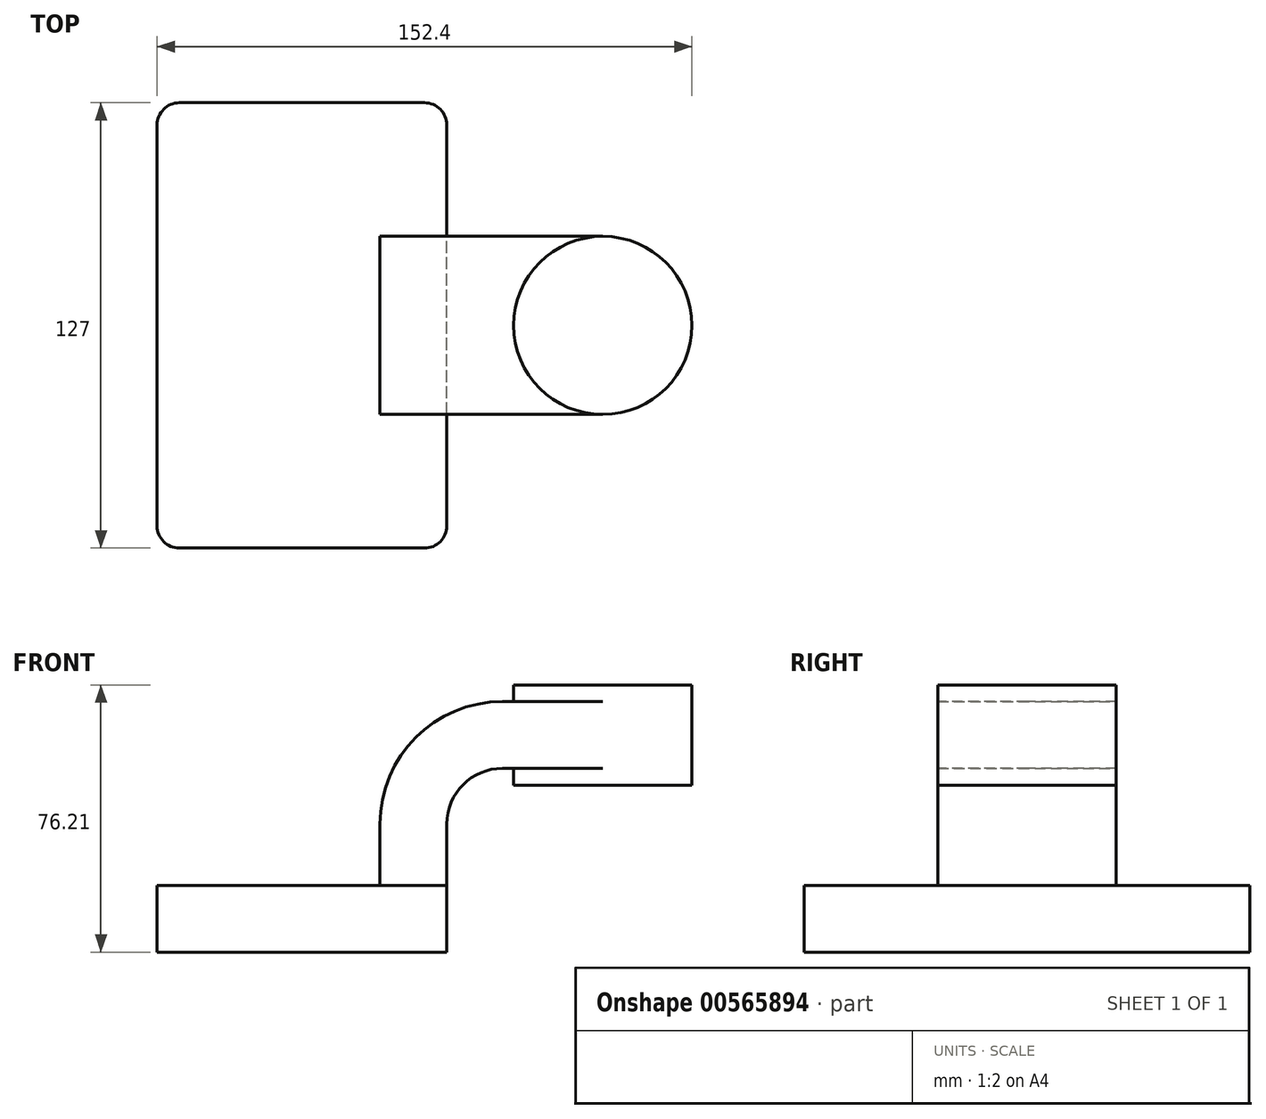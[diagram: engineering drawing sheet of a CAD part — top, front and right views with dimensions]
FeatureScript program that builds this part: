
annotation { "Feature Type Name" : "Feature", "Feature Type Description" : "" }
export const myFeature = defineFeature(function(context is Context, id is Id, definition is map)
    precondition{}
    {
        {
            var Q0;
            Q0=qCreatedBy(makeId("Front.planeOp"),FACE);
            var sketch = newSketch(context, id + "F0", { "sketchPlane" : qUnion([Q0])});
            skLineSegment(sketch, "E0.bottom", {"start": v(-41.28, -9.53) * mm, "end": v(41.28, -9.53) * mm});
            skLineSegment(sketch, "E0.top", {"start": v(-41.28, 9.52) * mm, "end": v(41.28, 9.52) * mm});
            skLineSegment(sketch, "E0.left", {"start": v(-41.28, -9.53) * mm, "end": v(-41.28, 9.52) * mm});
            skLineSegment(sketch, "E0.right", {"start": v(41.28, -9.53) * mm, "end": v(41.28, 9.52) * mm});
            skPoint(sketch, "E0.middle", {"position": v(0, 0) * mm});
            skLineSegment(sketch, "E1.bottom", {"start": v(60.32, 38.1) * mm, "end": v(111.12, 38.1) * mm});
            skLineSegment(sketch, "E1.top", {"start": v(60.32, 66.67) * mm, "end": v(111.12, 66.67) * mm});
            skLineSegment(sketch, "E1.left", {"start": v(60.32, 38.1) * mm, "end": v(60.32, 66.67) * mm});
            skLineSegment(sketch, "E1.right", {"start": v(111.12, 38.1) * mm, "end": v(111.12, 66.67) * mm});
            skPoint(sketch, "E1.middle", {"position": v(85.72, 52.39) * mm});
            skLineSegment(sketch, "E2", {"start": v(41.27, 9.52) * mm, "end": v(41.27, 27) * mm});
            skArc(sketch, "E3", {"start": v(41.27, 27) * mm, "mid": v(45.92, 38.23) * mm, "end": v(57.15, 42.88) * mm});
            skLineSegment(sketch, "E4", {"start": v(57.15, 42.88) * mm, "end": v(85.72, 42.88) * mm});
            skLineSegment(sketch, "E5.0", {"start": v(57.15, 61.93) * mm, "end": v(85.72, 61.93) * mm});
            skArc(sketch, "E5.1", {"start": v(22.22, 27) * mm, "mid": v(32.45, 51.7) * mm, "end": v(57.15, 61.93) * mm});
            skLineSegment(sketch, "E5.2", {"start": v(22.22, 9.52) * mm, "end": v(22.22, 27) * mm});
            skLineSegment(sketch, "E6", {"start": v(85.72, 38.1) * mm, "end": v(85.72, 66.67) * mm});
            skFitSpline(sketch, "E7", {"points": [v(-41.28, 9.53) * mm, v(57.15, 61.93) * mm], "startDerivative": vector(3.42, 82.2) * mm, "endDerivative": vector(203.54, -1.56) * mm});
            skSolve(sketch);
        }
        {
            var Q0;
            Q0=makeQuery(id+"F0.imprint","IMPRINT",FACE,{"disambiguationData":[TD([[makeQuery(id+"F0.imprint","IMPRINT",EDGE,{"derivedFrom":sQuery(id+"F0.wireOp",EDGE,"E0.bottom")}),1.0]])]});
            extrude(context, id + "F1", {"entities" : qUnion([Q0]), "endBound" : BoundingType.SYMMETRIC, "depth" : 127 * mm, "offsetDistance" : 25.4 * mm});
        }
        {
            var Q0;
            {var subQ1=sQuery(id+"F0.wireOp",EDGE,"E2");Q0=makeQuery(id+"F0.imprint","IMPRINT",FACE,{"disambiguationData":[TD([[makeQuery(id+"F0.imprint","IMPRINT",EDGE,{"derivedFrom":subQ1}),1.0]])]});}
            var Q1;
            {var subQ0=sQuery(id+"F0.wireOp",EDGE,"E4");var subQ1=sQuery(id+"F0.wireOp",EDGE,"E1.left");var subQ2=makeQuery(id+"F0.imprint","INTERSECT",VERTEX,{"derivedFrom":[subQ1,subQ0]});Q1=makeQuery(id+"F0.imprint","IMPRINT",FACE,{"disambiguationData":[TD([[makeQuery(id+"F0.imprint","IMPRINT",EDGE,{"disambiguationData":[TD([[subQ2,-1.0]])],"derivedFrom":subQ1}),-1.0]])]});}
            extrude(context, id + "F2", {"entities" : qUnion([Q0, Q1]), "endBound" : BoundingType.SYMMETRIC, "depth" : 50.8 * mm, "offsetDistance" : 25.4 * mm});
        }
        {
            var Q0;
            Q0=makeQuery(id+"F0.imprint","IMPRINT",FACE,{"disambiguationData":[TD([[makeQuery(id+"F0.imprint","IMPRINT",EDGE,{"derivedFrom":sQuery(id+"F0.wireOp",EDGE,"E5.1")}),1.0]])]});
            extrude(context, id + "F3", {"entities" : qUnion([Q0]), "endBound" : BoundingType.SYMMETRIC, "depth" : 15.88 * mm, "offsetDistance" : 25.4 * mm});
        }
        {
            var Q0;
            {var subQ0=sQuery(id+"F0.wireOp",EDGE,"E1.right");Q0=makeQuery(id+"F0.imprint","IMPRINT",FACE,{"disambiguationData":[TD([[makeQuery(id+"F0.imprint","IMPRINT",EDGE,{"derivedFrom":subQ0}),1.0]])]});}
            var Q1;
            Q1=sQuery(id+"F0.wireOp",EDGE,"E6");
            revolve(context, id + "F4", {"operationType" : NewBodyOperationType.ADD, "entities" : qUnion([Q0]), "axis" : qUnion([Q1]), "revolveType" : RevolveType.FULL});
        }
        {
            var Q0;
            Q0=makeQuery(id+"F1.opExtrude","CAP_EDGE",EDGE,{"disambiguationData":[OSD([sQuery(id+"F0.wireOp",EDGE,"E0.left")])],"isStart":false});
            var Q1;
            Q1=makeQuery(id+"F1.opExtrude","CAP_EDGE",EDGE,{"disambiguationData":[OSD([sQuery(id+"F0.wireOp",EDGE,"E0.right")])],"isStart":false});
            var Q2;
            Q2=makeQuery(id+"F1.opExtrude","CAP_EDGE",EDGE,{"disambiguationData":[OSD([sQuery(id+"F0.wireOp",EDGE,"E0.left")])],"isStart":true});
            var Q3;
            Q3=makeQuery(id+"F1.opExtrude","CAP_EDGE",EDGE,{"disambiguationData":[OSD([sQuery(id+"F0.wireOp",EDGE,"E0.right")])],"isStart":true});
            fillet(context, id + "F5", {"entities" : qUnion([Q0, Q1, Q2, Q3]), "radius" : 6.35 * mm, "tangentPropagation" : true, "allowEdgeOverflow" : false});
        }
    });
